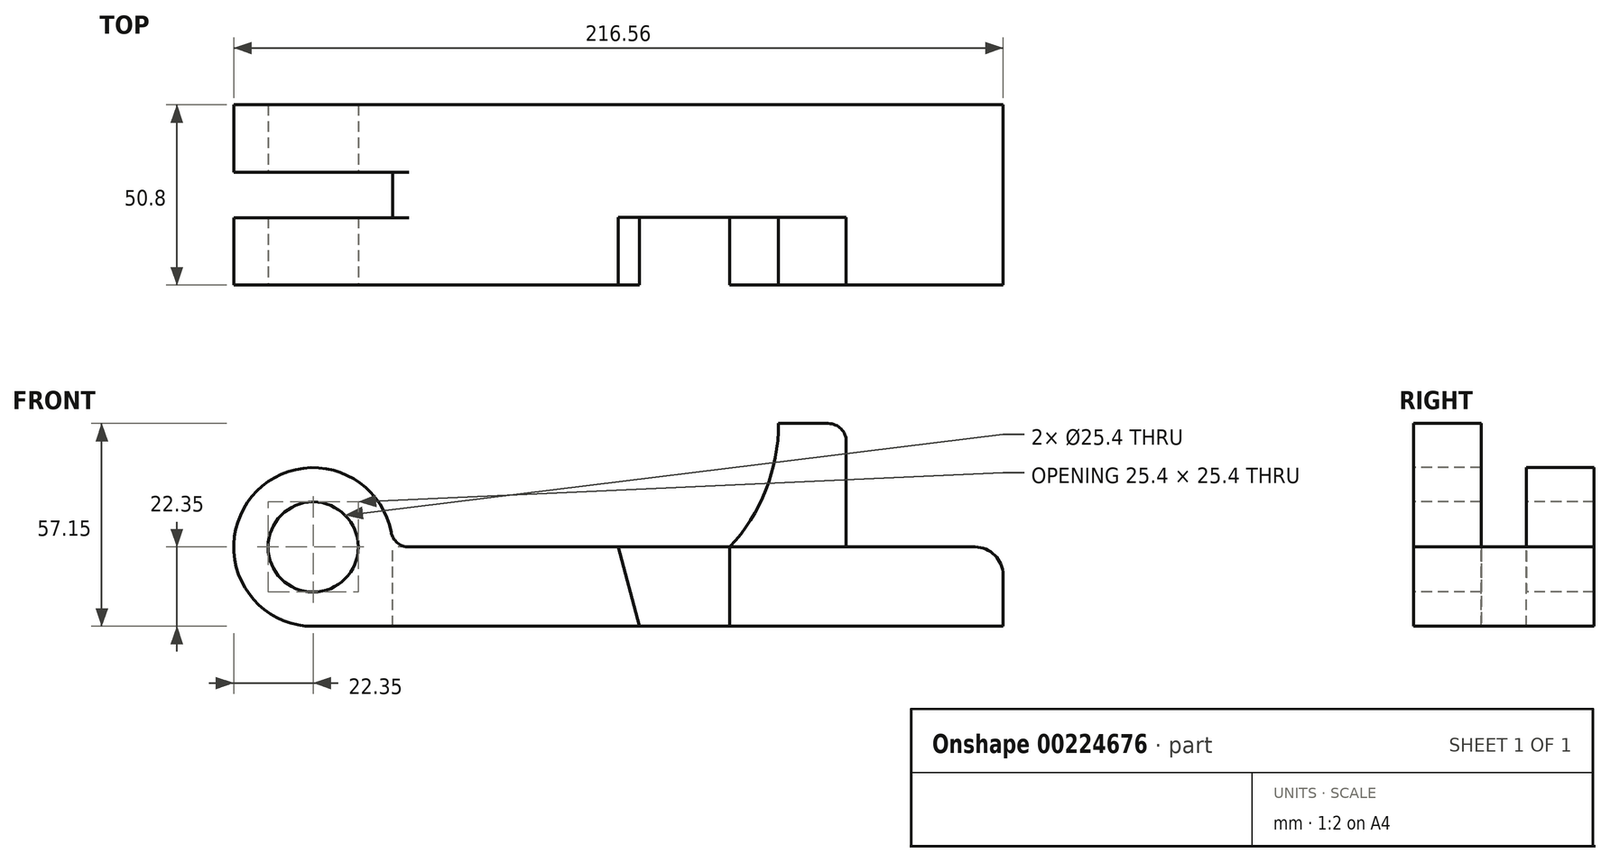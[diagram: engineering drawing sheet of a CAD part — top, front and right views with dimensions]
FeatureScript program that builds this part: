
annotation { "Feature Type Name" : "Feature", "Feature Type Description" : "" }
export const myFeature = defineFeature(function(context is Context, id is Id, definition is map)
    precondition{}
    {
        {
            var Q0;
            Q0=qCreatedBy(makeId("Front.planeOp"),FACE);
            var sketch = newSketch(context, id + "F0", { "sketchPlane" : qUnion([Q0])});
            skLineSegment(sketch, "E0.top", {"start": v(0, -22.35) * mm, "end": v(117.25, -22.35) * mm});
            skLineSegment(sketch, "E0.left", {"start": v(0, 0) * mm, "end": v(0, -12.7) * mm});
            skLineSegment(sketch, "E0.right", {"start": v(117.25, 0) * mm, "end": v(117.25, -22.35) * mm});
            skCircle(sketch, "E1", {"center": v(0, 0) * mm, "radius": 12.7 * mm});
            skArc(sketch, "E2", {"start": v(22.35, 0) * mm, "mid": v(-15.8, 15.8) * mm, "end": v(0, -22.35) * mm});
            skLineSegment(sketch, "E3.trimOffspring", {"start": v(22.35, 0) * mm, "end": v(117.25, 0) * mm});
            skLineSegment(sketch, "E4", {"start": v(0, 0) * mm, "end": v(85.85, 0) * mm});
            skLineSegment(sketch, "E5", {"start": v(0, -22.35) * mm, "end": v(91.85, -22.35) * mm});
            skLineSegment(sketch, "E6", {"start": v(85.85, 0) * mm, "end": v(91.85, -22.35) * mm});
            skLineSegment(sketch, "E7", {"start": v(117.25, -22.35) * mm, "end": v(194.2, -22.35) * mm});
            skLineSegment(sketch, "E8", {"start": v(194.2, -22.35) * mm, "end": v(194.2, 0) * mm});
            skLineSegment(sketch, "E9", {"start": v(194.2, 0) * mm, "end": v(150.09, 0) * mm});
            skLineSegment(sketch, "E10", {"start": v(150.09, 0) * mm, "end": v(150.09, 34.8) * mm});
            skLineSegment(sketch, "E11", {"start": v(150.09, 34.8) * mm, "end": v(131.04, 34.8) * mm});
            skArc(sketch, "E12", {"start": v(117.25, 0) * mm, "mid": v(127.46, 16.08) * mm, "end": v(131.04, 34.8) * mm});
            skLineSegment(sketch, "E13", {"start": v(117.25, 0) * mm, "end": v(150.09, 0) * mm});
            skSolve(sketch);
        }
        {
            var Q0;
            Q0=makeQuery(id+"F0.imprint","IMPRINT",FACE,{"disambiguationData":[TD([[makeQuery(id+"F0.imprint","IMPRINT",EDGE,{"derivedFrom":sQuery(id+"F0.wireOp",EDGE,"E0.right")}),1.0]])]});
            var Q1;
            Q1=makeQuery(id+"F0.imprint","IMPRINT",FACE,{"disambiguationData":[TD([[makeQuery(id+"F0.imprint","IMPRINT",EDGE,{"derivedFrom":sQuery(id+"F0.wireOp",EDGE,"E0.top")}),1.0]])]});
            var Q2;
            {var subQ1=sQuery(id+"F0.wireOp",EDGE,"E2");Q2=makeQuery(id+"F0.imprint","IMPRINT",FACE,{"disambiguationData":[TD([[makeQuery(id+"F0.imprint","IMPRINT",EDGE,{"derivedFrom":subQ1}),1.0]])]});}
            extrude(context, id + "F1", {"entities" : qUnion([Q0, Q1, Q2]), "oppositeDirection" : true, "depth" : 50.8 * mm});
        }
        {
            var Q0;
            Q0=makeQuery(id+"F0.imprint","IMPRINT",FACE,{"disambiguationData":[TD([[makeQuery(id+"F0.imprint","IMPRINT",EDGE,{"derivedFrom":sQuery(id+"F0.wireOp",EDGE,"E10")}),1.0]])]});
            extrude(context, id + "F2", {"entities" : qUnion([Q0]), "oppositeDirection" : true, "depth" : 19.05 * mm});
        }
        {
            var Q0;
            Q0=makeQuery(id+"F0.imprint","IMPRINT",FACE,{"disambiguationData":[TD([[makeQuery(id+"F0.imprint","IMPRINT",EDGE,{"derivedFrom":sQuery(id+"F0.wireOp",EDGE,"E0.top")}),1.0]])]});
            extrude(context, id + "F3", {"entities" : qUnion([Q0]), "operationType" : NewBodyOperationType.REMOVE, "oppositeDirection" : true, "depth" : 19.05 * mm});
        }
        {
            var Q0;
            Q0=makeQuery(id+"F1.opExtrude","SWEPT_FACE",FACE,{"disambiguationData":[OSD([sQuery(id+"F0.wireOp",EDGE,"E3.trimOffspring"),sQuery(id+"F0.wireOp",EDGE,"E4"),sQuery(id+"F0.wireOp",EDGE,"E9"),sQuery(id+"F0.wireOp",EDGE,"E13")])]});
            var sketch = newSketch(context, id + "F4", { "sketchPlane" : qUnion([Q0])});
            skLineSegment(sketch, "E14.bottom", {"start": v(22.35, 19) * mm, "end": v(-28.57, 19) * mm});
            skLineSegment(sketch, "E14.top", {"start": v(22.35, 31.8) * mm, "end": v(-28.57, 31.8) * mm});
            skLineSegment(sketch, "E14.left", {"start": v(22.35, 19) * mm, "end": v(22.35, 31.8) * mm});
            skLineSegment(sketch, "E14.right", {"start": v(-28.57, 19) * mm, "end": v(-28.57, 31.8) * mm});
            skPoint(sketch, "E14.middle", {"position": v(-3.11, 25.4) * mm});
            skPoint(sketch, "E14.middle.positionSnap0", {"position": v(22.35, 25.4) * mm});
            skPoint(sketch, "E14.centerSnap0", {"position": v(22.35, 25.4) * mm});
            skSolve(sketch);
        }
        {
            var Q0;
            Q0=makeQuery(id+"F4.imprint","IMPRINT",FACE,{"disambiguationData":[TD([[makeQuery(id+"F4.imprint","IMPRINT",EDGE,{"derivedFrom":sQuery(id+"F4.wireOp",EDGE,"E14.bottom")}),-1.0]])]});
            extrude(context, id + "F5", {"entities" : qUnion([Q0]), "operationType" : NewBodyOperationType.REMOVE, "endBound" : BoundingType.SYMMETRIC, "oppositeDirection" : true, "depth" : 50.8 * mm});
        }
        {
            var Q0;
            {var subQ0=sQuery(id+"F0.wireOp",EDGE,"E13");var subQ1=sQuery(id+"F0.wireOp",EDGE,"E9");var subQ2=sQuery(id+"F0.wireOp",EDGE,"E4");var subQ3=sQuery(id+"F0.wireOp",EDGE,"E3.trimOffspring");var subQ4=sQuery(id+"F0.wireOp",EDGE,"E2");Q0=makeQuery(id+"F5.boolean.opBoolean","SPLIT",EDGE,{"disambiguationData":[TD([makeQuery(id+"F1.opExtrude","CAP_FACE",FACE,{"disambiguationData":[OSD([sQuery(id+"F0.wireOp",EDGE,"E0.top"),sQuery(id+"F0.wireOp",EDGE,"E1"),subQ4,subQ3,subQ2,sQuery(id+"F0.wireOp",EDGE,"E5"),sQuery(id+"F0.wireOp",EDGE,"E7"),sQuery(id+"F0.wireOp",EDGE,"E8"),subQ1,subQ0])],"isStart":true}),makeQuery(id+"F1.opExtrude","SWEPT_FACE",FACE,{"disambiguationData":[OSD([subQ4])]}),makeQuery(id+"F1.opExtrude","SWEPT_FACE",FACE,{"disambiguationData":[OSD([subQ3,subQ2,subQ1,subQ0])]}),makeQuery(id+"F5.opExtrude","SWEPT_FACE",FACE,{"disambiguationData":[OSD([sQuery(id+"F4.wireOp",EDGE,"E14.bottom")])]}),makeQuery(id+"F5.opExtrude","SWEPT_FACE",FACE,{"disambiguationData":[OSD([sQuery(id+"F4.wireOp",EDGE,"E14.left")])]})])],"derivedFrom":makeQuery(id+"F1.opExtrude","SWEPT_EDGE",EDGE,{"disambiguationData":[OSD([subQ4,subQ2])]})});}
            var Q1;
            {var subQ0=sQuery(id+"F0.wireOp",EDGE,"E13");var subQ1=sQuery(id+"F0.wireOp",EDGE,"E9");var subQ2=sQuery(id+"F0.wireOp",EDGE,"E4");var subQ3=sQuery(id+"F0.wireOp",EDGE,"E3.trimOffspring");var subQ4=sQuery(id+"F0.wireOp",EDGE,"E2");Q1=makeQuery(id+"F5.boolean.opBoolean","SPLIT",EDGE,{"disambiguationData":[TD([makeQuery(id+"F1.opExtrude","CAP_FACE",FACE,{"disambiguationData":[OSD([sQuery(id+"F0.wireOp",EDGE,"E0.top"),sQuery(id+"F0.wireOp",EDGE,"E1"),subQ4,subQ3,subQ2,sQuery(id+"F0.wireOp",EDGE,"E5"),sQuery(id+"F0.wireOp",EDGE,"E7"),sQuery(id+"F0.wireOp",EDGE,"E8"),subQ1,subQ0])],"isStart":false}),makeQuery(id+"F1.opExtrude","SWEPT_FACE",FACE,{"disambiguationData":[OSD([subQ4])]}),makeQuery(id+"F1.opExtrude","SWEPT_FACE",FACE,{"disambiguationData":[OSD([subQ3,subQ2,subQ1,subQ0])]}),makeQuery(id+"F5.opExtrude","SWEPT_FACE",FACE,{"disambiguationData":[OSD([sQuery(id+"F4.wireOp",EDGE,"E14.top")])]}),makeQuery(id+"F5.opExtrude","SWEPT_FACE",FACE,{"disambiguationData":[OSD([sQuery(id+"F4.wireOp",EDGE,"E14.left")])]})])],"derivedFrom":makeQuery(id+"F1.opExtrude","SWEPT_EDGE",EDGE,{"disambiguationData":[OSD([subQ4,subQ2])]})});}
            fillet(context, id + "F6", {"entities" : qUnion([Q0, Q1]), "radius" : 5.08 * mm, "tangentPropagation" : true, "allowEdgeOverflow" : false});
        }
        {
            var Q0;
            Q0=makeQuery(id+"F1.opExtrude","SWEPT_EDGE",EDGE,{"disambiguationData":[OSD([sQuery(id+"F0.wireOp",EDGE,"E8"),sQuery(id+"F0.wireOp",EDGE,"E9")])]});
            fillet(context, id + "F7", {"entities" : qUnion([Q0]), "radius" : 7.87 * mm, "tangentPropagation" : true, "allowEdgeOverflow" : false});
        }
        {
            var Q0;
            Q0=makeQuery(id+"F2.opExtrude","SWEPT_EDGE",EDGE,{"disambiguationData":[OSD([sQuery(id+"F0.wireOp",EDGE,"E10"),sQuery(id+"F0.wireOp",EDGE,"E11")])]});
            fillet(context, id + "F8", {"entities" : qUnion([Q0]), "radius" : 5.08 * mm, "tangentPropagation" : true, "allowEdgeOverflow" : false});
        }
    });
